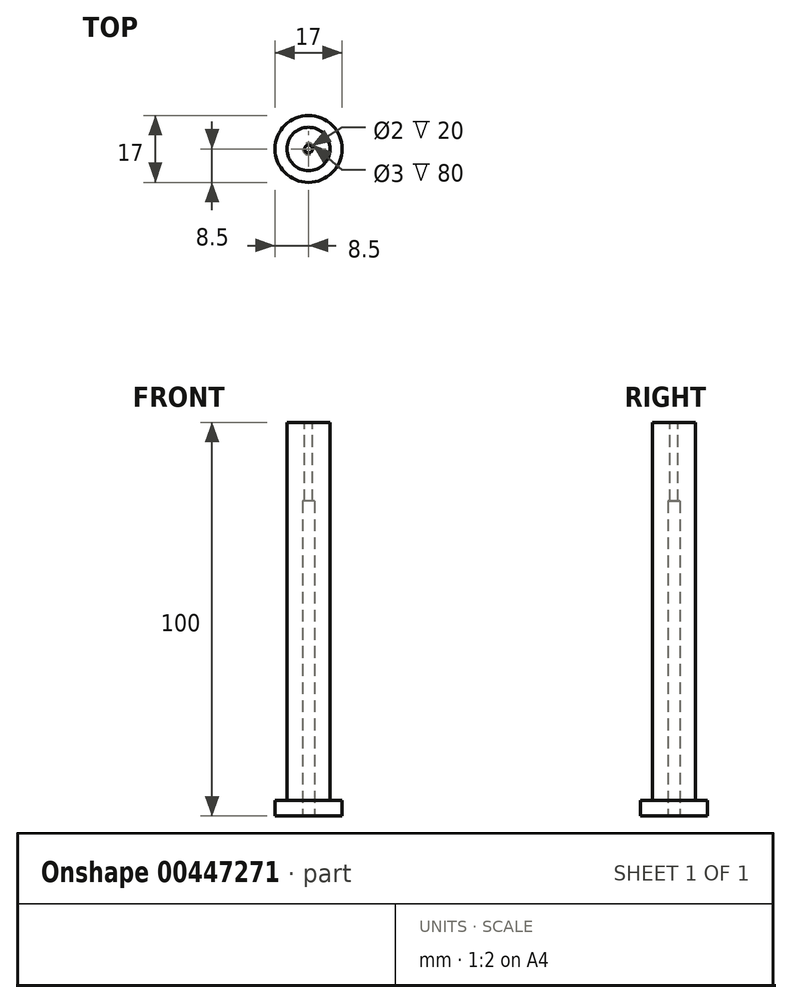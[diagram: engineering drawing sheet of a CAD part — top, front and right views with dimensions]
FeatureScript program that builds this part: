
annotation { "Feature Type Name" : "Feature", "Feature Type Description" : "" }
export const myFeature = defineFeature(function(context is Context, id is Id, definition is map)
    precondition{}
    {
        {
            var Q0;
            Q0=qCreatedBy(makeId("Top.planeOp"),FACE);
            var sketch = newSketch(context, id + "F0", { "sketchPlane" : qUnion([Q0])});
            skCircle(sketch, "E0", {"center": v(0, 0) * mm, "radius": 8.5 * mm});
            skSolve(sketch);
        }
        {
            var Q0;
            Q0=qSketchRegion(id+"F0",true);
            extrude(context, id + "F1", {"entities" : qUnion([Q0]), "depth" : 4 * mm});
        }
        {
            var Q0;
            Q0=qCreatedBy(makeId("Top.planeOp"),FACE);
            var sketch = newSketch(context, id + "F2", { "sketchPlane" : qUnion([Q0])});
            skCircle(sketch, "E1", {"center": v(0, 0) * mm, "radius": 5.5 * mm});
            skSolve(sketch);
        }
        {
            var Q0;
            Q0=qSketchRegion(id+"F2",true);
            extrude(context, id + "F3", {"entities" : qUnion([Q0]), "operationType" : NewBodyOperationType.ADD, "depth" : 100 * mm});
        }
        {
            var Q0;
            Q0=makeQuery(id+"F3.opExtrude","CAP_FACE",FACE,{"disambiguationData":[OSD([sQuery(id+"F2.wireOp",EDGE,"E1")])],"isStart":false});
            var sketch = newSketch(context, id + "F4", { "sketchPlane" : qUnion([Q0])});
            skCircle(sketch, "E2", {"center": v(0, 0) * mm, "radius": 1 * mm});
            skSolve(sketch);
        }
        {
            var Q0;
            Q0=makeQuery(id+"F4.imprint","IMPRINT",FACE,{"disambiguationData":[TD([[makeQuery(id+"F4.imprint","IMPRINT",EDGE,{"derivedFrom":sQuery(id+"F4.wireOp",EDGE,"E2")}),1.0]])]});
            extrude(context, id + "F5", {"entities" : qUnion([Q0]), "operationType" : NewBodyOperationType.REMOVE, "oppositeDirection" : true, "depth" : 114.9 * mm});
        }
        {
            var Q0;
            Q0=qCreatedBy(makeId("Top.planeOp"),FACE);
            var sketch = newSketch(context, id + "F6", { "sketchPlane" : qUnion([Q0])});
            skCircle(sketch, "E3", {"center": v(0, 0) * mm, "radius": 1.5 * mm});
            skSolve(sketch);
        }
        {
            var Q0;
            Q0=makeQuery(id+"F6.imprint","IMPRINT",FACE,{"disambiguationData":[TD([[makeQuery(id+"F6.imprint","IMPRINT",EDGE,{"derivedFrom":sQuery(id+"F6.wireOp",EDGE,"E3")}),1.0]])]});
            extrude(context, id + "F7", {"entities" : qUnion([Q0]), "operationType" : NewBodyOperationType.REMOVE, "depth" : 80 * mm});
        }
    });
